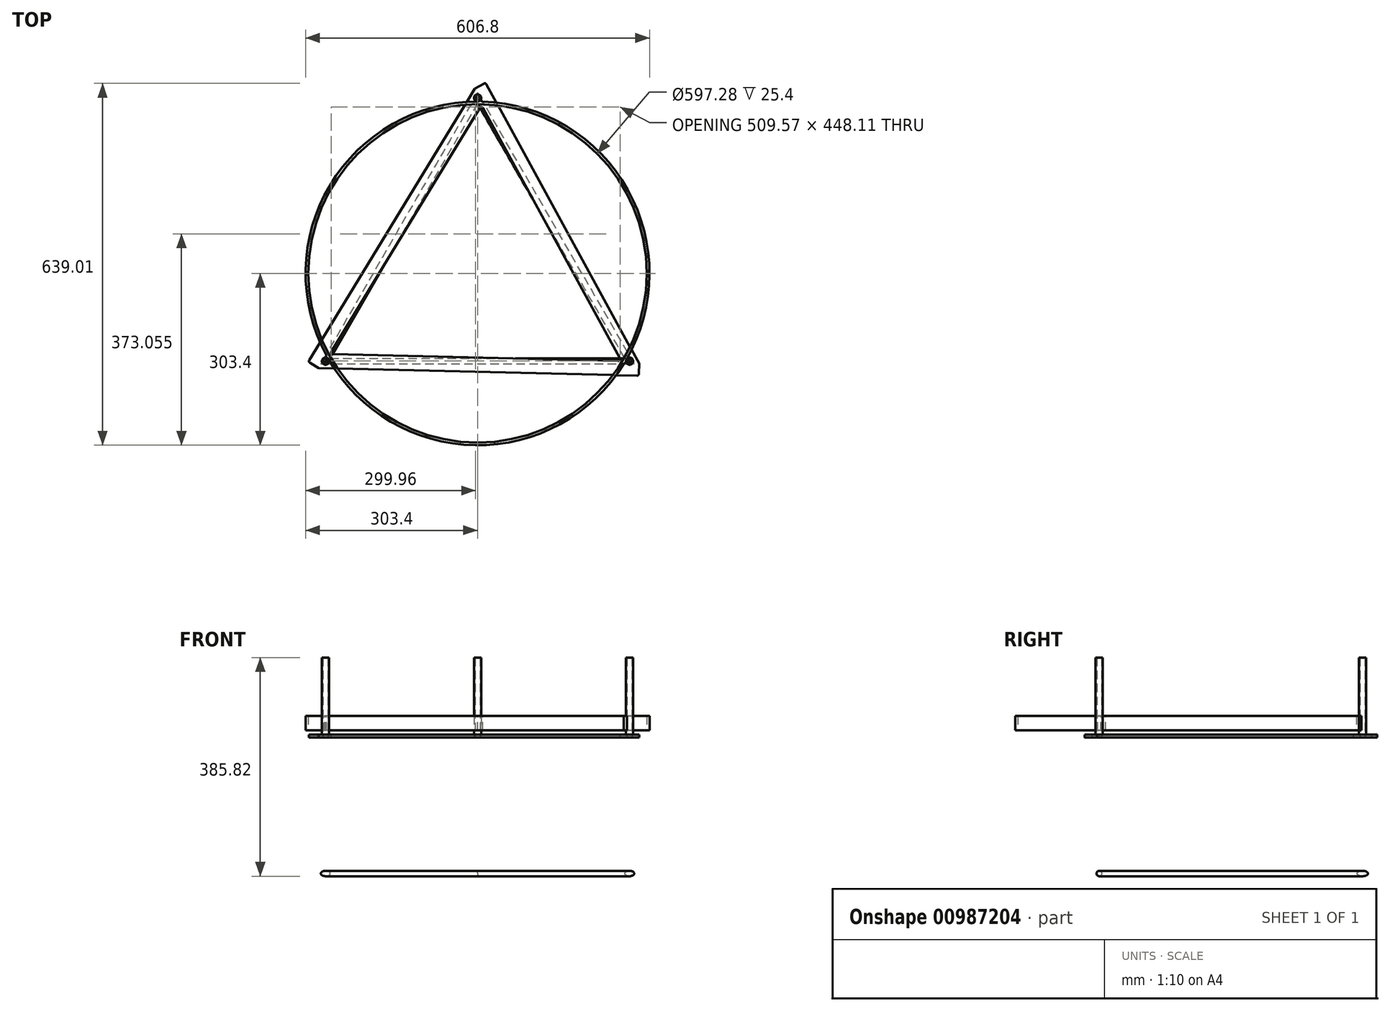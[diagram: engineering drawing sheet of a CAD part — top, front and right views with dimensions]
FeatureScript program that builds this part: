
annotation { "Feature Type Name" : "Feature", "Feature Type Description" : "" }
export const myFeature = defineFeature(function(context is Context, id is Id, definition is map)
    precondition{}
    {
        {
            var Q0;
            Q0=qCreatedBy(makeId("Top.planeOp"),FACE);
            var sketch = newSketch(context, id + "F0", { "sketchPlane" : qUnion([Q0])});
            skCircle(sketch, "E0", {"center": v(0, 0) * mm, "radius": 303.4 * mm});
            skCircle(sketch, "E1.0", {"center": v(0, 0) * mm, "radius": 298.64 * mm});
            skSolve(sketch);
        }
        {
            var Q0;
            Q0=makeQuery(id+"F0.imprint","IMPRINT",FACE,{"disambiguationData":[TD([[makeQuery(id+"F0.imprint","IMPRINT",EDGE,{"derivedFrom":sQuery(id+"F0.wireOp",EDGE,"E0")}),1.0]])]});
            extrude(context, id + "F1", {"entities" : qUnion([Q0]), "depth" : 25.4 * mm, "offsetDistance" : 25.4 * mm});
        }
        {
            var Q0;
            Q0=makeQuery(id+"F1.opExtrude","CAP_FACE",FACE,{"disambiguationData":[OSD([sQuery(id+"F0.wireOp",EDGE,"E0"),sQuery(id+"F0.wireOp",EDGE,"E1.0")])],"isStart":false});
            var sketch = newSketch(context, id + "F2", { "sketchPlane" : qUnion([Q0])});
            skLineSegment(sketch, "E2", {"start": v(0, 0) * mm, "end": v(0, 365.8) * mm});
            skLineSegment(sketch, "E3.1.0", {"start": v(0, 0) * mm, "end": v(-316.8, -182.9) * mm});
            skLineSegment(sketch, "E3.2.0", {"start": v(0, 0) * mm, "end": v(316.8, -182.9) * mm});
            skPoint(sketch, "E3.center", {"position": v(0, 0) * mm});
            skCircle(sketch, "E4", {"center": v(0, 309.75) * mm, "radius": 6.35 * mm});
            skCircle(sketch, "E5.1.0", {"center": v(-268.25, -154.88) * mm, "radius": 6.35 * mm});
            skCircle(sketch, "E5.2.0", {"center": v(268.25, -154.88) * mm, "radius": 6.35 * mm});
            skCircle(sketch, "E6.0", {"center": v(0, 309.75) * mm, "radius": 4.32 * mm});
            skCircle(sketch, "E7.1.0", {"center": v(-268.25, -154.88) * mm, "radius": 4.32 * mm});
            skCircle(sketch, "E7.2.0", {"center": v(268.25, -154.88) * mm, "radius": 4.32 * mm});
            skSolve(sketch);
        }
        {
            var Q0;
            {var subQ1=sQuery(id+"F2.wireOp",EDGE,"E2");var subQ3=sQuery(id+"F2.wireOp",EDGE,"E4");var subQ5=makeQuery(id+"F2.imprint","INTERSECT",VERTEX,{"derivedFrom":[subQ1,subQ3]});Q0=makeQuery(id+"F2.imprint","IMPRINT",FACE,{"disambiguationData":[TD([[makeQuery(id+"F2.imprint","IMPRINT",EDGE,{"disambiguationData":[TD([[subQ5,1.0]])],"derivedFrom":subQ1}),1.0]])]});}
            var Q1;
            {var subQ1=sQuery(id+"F2.wireOp",EDGE,"E2");var subQ3=sQuery(id+"F2.wireOp",EDGE,"E4");var subQ6=makeQuery(id+"F2.imprint","INTERSECT",VERTEX,{"derivedFrom":[subQ1,subQ3]});Q1=makeQuery(id+"F2.imprint","IMPRINT",FACE,{"disambiguationData":[TD([[makeQuery(id+"F2.imprint","IMPRINT",EDGE,{"disambiguationData":[TD([[subQ6,1.0]])],"derivedFrom":subQ1}),-1.0]])]});}
            var Q2;
            {var subQ1=sQuery(id+"F2.wireOp",EDGE,"E3.2.0");var subQ3=sQuery(id+"F2.wireOp",EDGE,"E5.2.0");var subQ5=makeQuery(id+"F2.imprint","INTERSECT",VERTEX,{"derivedFrom":[subQ1,subQ3]});Q2=makeQuery(id+"F2.imprint","IMPRINT",FACE,{"disambiguationData":[TD([[makeQuery(id+"F2.imprint","IMPRINT",EDGE,{"disambiguationData":[TD([[subQ5,1.0]])],"derivedFrom":subQ1}),-1.0]])]});}
            var Q3;
            {var subQ1=sQuery(id+"F2.wireOp",EDGE,"E3.2.0");var subQ3=sQuery(id+"F2.wireOp",EDGE,"E5.2.0");var subQ5=makeQuery(id+"F2.imprint","INTERSECT",VERTEX,{"derivedFrom":[subQ1,subQ3]});Q3=makeQuery(id+"F2.imprint","IMPRINT",FACE,{"disambiguationData":[TD([[makeQuery(id+"F2.imprint","IMPRINT",EDGE,{"disambiguationData":[TD([[subQ5,1.0]])],"derivedFrom":subQ1}),1.0]])]});}
            var Q4;
            {var subQ1=sQuery(id+"F2.wireOp",EDGE,"E3.1.0");var subQ3=sQuery(id+"F2.wireOp",EDGE,"E5.1.0");var subQ5=makeQuery(id+"F2.imprint","INTERSECT",VERTEX,{"derivedFrom":[subQ1,subQ3]});Q4=makeQuery(id+"F2.imprint","IMPRINT",FACE,{"disambiguationData":[TD([[makeQuery(id+"F2.imprint","IMPRINT",EDGE,{"disambiguationData":[TD([[subQ5,1.0]])],"derivedFrom":subQ1}),-1.0]])]});}
            var Q5;
            {var subQ1=sQuery(id+"F2.wireOp",EDGE,"E3.1.0");var subQ3=sQuery(id+"F2.wireOp",EDGE,"E5.1.0");var subQ5=makeQuery(id+"F2.imprint","INTERSECT",VERTEX,{"derivedFrom":[subQ1,subQ3]});Q5=makeQuery(id+"F2.imprint","IMPRINT",FACE,{"disambiguationData":[TD([[makeQuery(id+"F2.imprint","IMPRINT",EDGE,{"disambiguationData":[TD([[subQ5,1.0]])],"derivedFrom":subQ1}),1.0]])]});}
            extrude(context, id + "F3", {"entities" : qUnion([Q0, Q1, Q2, Q3, Q4, Q5]), "depth" : 103.12 * mm, "offsetDistance" : 25.4 * mm, "hasSecondDirection" : true, "secondDirectionOppositeDirection" : true, "secondDirectionDepth" : (33.13 - (3 / 16)) * mm});
        }
        {
            var Q0;
            Q0=makeQuery(id+"F1.opExtrude","CAP_FACE",FACE,{"disambiguationData":[OSD([sQuery(id+"F0.wireOp",EDGE,"E0"),sQuery(id+"F0.wireOp",EDGE,"E1.0")])],"isStart":false});
            var sketch = newSketch(context, id + "F4", { "sketchPlane" : qUnion([Q0])});
            skArc(sketch, "E8.0", {"start": v(-267.31, -143.52) * mm, "mid": v(-265.06, -147.63) * mm, "end": v(-262.75, -151.7) * mm});
            skCircle(sketch, "E9.0", {"center": v(-268.25, -154.88) * mm, "radius": 6.35 * mm});
            skLineSegment(sketch, "E10", {"start": v(-268.25, -154.88) * mm, "end": v(0, 0) * mm});
            skArc(sketch, "E11", {"start": v(-269.4, -148.63) * mm, "mid": v(-267.08, -146.6) * mm, "end": v(-267.3, -143.52) * mm});
            skLineSegment(sketch, "E12", {"start": v(-267.3, -143.52) * mm, "end": v(-267.31, -143.52) * mm});
            skLineSegment(sketch, "E13", {"start": v(-267.31, -143.52) * mm, "end": v(-267.3, -143.52) * mm});
            skLineSegment(sketch, "E14.MirrorCS", {"start": v(-257.95, -159.74) * mm, "end": v(-257.95, -159.74) * mm});
            skArc(sketch, "E15.MirrorCS", {"start": v(-263.42, -159) * mm, "mid": v(-260.5, -158) * mm, "end": v(-257.95, -159.74) * mm});
            skArc(sketch, "E16.MirrorCS", {"start": v(-257.95, -159.74) * mm, "mid": v(-260.38, -155.74) * mm, "end": v(-262.75, -151.7) * mm});
            skSolve(sketch);
        }
        {
            var Q0;
            {var subQ0=sQuery(id+"F4.wireOp",EDGE,"E9.0");var subQ1=sQuery(id+"F4.wireOp",EDGE,"E11");var subQ2=makeQuery(id+"F4.imprint","INTERSECT",VERTEX,{"derivedFrom":[subQ1,subQ0]});Q0=makeQuery(id+"F4.imprint","IMPRINT",FACE,{"disambiguationData":[TD([[makeQuery(id+"F4.imprint","IMPRINT",EDGE,{"disambiguationData":[TD([[subQ2,-1.0]])],"derivedFrom":subQ1}),-1.0]])]});}
            var Q1;
            {var subQ0=sQuery(id+"F4.wireOp",EDGE,"E9.0");var subQ1=sQuery(id+"F4.wireOp",EDGE,"E15.MirrorCS");var subQ2=makeQuery(id+"F4.imprint","INTERSECT",VERTEX,{"derivedFrom":[subQ1,subQ0]});Q1=makeQuery(id+"F4.imprint","IMPRINT",FACE,{"disambiguationData":[TD([[makeQuery(id+"F4.imprint","IMPRINT",EDGE,{"disambiguationData":[TD([[subQ2,-1.0]])],"derivedFrom":subQ1}),1.0]])]});}
            var Q2;
            Q2=makeQuery(id+"F1.opExtrude","CAP_FACE",FACE,{"disambiguationData":[OSD([sQuery(id+"F0.wireOp",EDGE,"E0"),sQuery(id+"F0.wireOp",EDGE,"E1.0")])],"isStart":true});
            extrude(context, id + "F5", {"entities" : qUnion([Q0, Q1]), "endBound" : BoundingType.UP_TO_SURFACE, "oppositeDirection" : true, "depth" : 25.4 * mm, "endBoundEntityFace" : qUnion([Q2]), "offsetDistance" : 25.4 * mm});
        }
        {
            var Q0;
            Q0=qCreatedBy(makeId("Right.planeOp"),FACE);
            var sketch = newSketch(context, id + "F6", { "sketchPlane" : qUnion([Q0])});
            skLineSegment(sketch, "E17", {"start": v(0, 0) * mm, "end": v(0, 80.11) * mm});
            skSolve(sketch);
        }
        {
            var Q0;
            Q0=makeQuery(id+"F5.opExtrude","SWEPT_BODY",BODY,{"disambiguationData":[OSD([sQuery(id+"F4.wireOp",EDGE,"E15.MirrorCS"),sQuery(id+"F4.wireOp",EDGE,"E16.MirrorCS"),sQuery(id+"F4.wireOp",EDGE,"E9.0")])]});
            var Q1;
            Q1=makeQuery(id+"F5.opExtrude","SWEPT_BODY",BODY,{"disambiguationData":[OSD([sQuery(id+"F4.wireOp",EDGE,"E11"),sQuery(id+"F4.wireOp",EDGE,"E8.0"),sQuery(id+"F4.wireOp",EDGE,"E9.0")])]});
            var Q2;
            Q2=sQuery(id+"F6.wireOp",EDGE,"E17");
            circularPattern(context, id + "F7", {"operationType" : NewBodyOperationType.ADD, "entities" : qUnion([Q0, Q1]), "axis" : qUnion([Q2]), "angle" : 360 * degree, "instanceCount" : 3, "equalSpace" : true});
        }
        {
            var Q0;
            Q0=makeQuery(id+"F3.opExtrude","CAP_FACE",FACE,{"disambiguationData":[OSD([sQuery(id+"F2.wireOp",EDGE,"E5.2.0"),sQuery(id+"F2.wireOp",EDGE,"E7.2.0")])],"isStart":true});
            var sketch = newSketch(context, id + "F8", { "sketchPlane" : qUnion([Q0])});
            skLineSegment(sketch, "E18.bottom", {"start": v(-280.31, 167.3) * mm, "end": v(281.35, 180.6) * mm});
            skLineSegment(sketch, "E18.top", {"start": v(-255.13, 142.48) * mm, "end": v(248.1, 154.4) * mm});
            skLineSegment(sketch, "E18.right", {"start": v(284.6, 177.5) * mm, "end": v(285.04, 159.11) * mm});
            skCircle(sketch, "E19.0", {"center": v(-268.25, 154.88) * mm, "radius": 4.32 * mm});
            skCircle(sketch, "E20.0", {"center": v(268.25, 154.88) * mm, "radius": 4.32 * mm});
            skPoint(sketch, "E21.center", {"position": v(3.6, 6.4) * mm});
            skLineSegment(sketch, "E22.1.0", {"start": v(4.17, -292.19) * mm, "end": v(-257.76, 137.66) * mm});
            skLineSegment(sketch, "E22.1.1", {"start": v(-4.72, -326.4) * mm, "end": v(-297.08, 153.36) * mm});
            skCircle(sketch, "E22.1.3", {"center": v(0, -309.75) * mm, "radius": 4.32 * mm});
            skLineSegment(sketch, "E22.1.4", {"start": v(-296.02, 157.73) * mm, "end": v(-280.31, 167.3) * mm});
            skLineSegment(sketch, "E22.2.0", {"start": v(250.96, 149.7) * mm, "end": v(9.67, -292.06) * mm});
            skLineSegment(sketch, "E22.2.1", {"start": v(285.04, 159.11) * mm, "end": v(15.72, -333.96) * mm});
            skCircle(sketch, "E22.2.2", {"center": v(0, -309.75) * mm, "radius": 4.32 * mm});
            skLineSegment(sketch, "E22.2.4", {"start": v(11.41, -335.22) * mm, "end": v(-4.72, -326.4) * mm});
            skPoint(sketch, "E22.center", {"position": v(0, 0) * mm});
            skPoint(sketch, "E23.orphan", {"position": v(-285.29, 167.18) * mm});
            skPoint(sketch, "E24.orphan", {"position": v(-277.04, 169.3) * mm});
            skLineSegment(sketch, "E25.trimOffspring", {"start": v(-268.25, 154.88) * mm, "end": v(-270.5, 158.56) * mm});
            skPoint(sketch, "E26.orphan", {"position": v(265.13, 175.65) * mm});
            skPoint(sketch, "E27.orphan", {"position": v(287.42, 163.48) * mm});
            skPoint(sketch, "E28.orphan", {"position": v(285.13, 155.28) * mm});
            skLineSegment(sketch, "E29.trimOffspring", {"start": v(268.25, 154.88) * mm, "end": v(272.57, 154.98) * mm});
            skPoint(sketch, "E30.orphan", {"position": v(19.56, -317.44) * mm});
            skLineSegment(sketch, "E31.trimOffspring", {"start": v(2.07, -305.96) * mm, "end": v(0, -309.75) * mm});
            skPoint(sketch, "E32.visualSharp", {"position": v(-260.62, 142.35) * mm});
            skArc(sketch, "E32.filletArc", {"start": v(-255.13, 142.48) * mm, "mid": v(-257.84, 140.83) * mm, "end": v(-257.76, 137.66) * mm});
            skPoint(sketch, "E33.visualSharp", {"position": v(-298.73, 156.07) * mm});
            skArc(sketch, "E33.filletArc", {"start": v(-296.02, 157.73) * mm, "mid": v(-297.45, 155.76) * mm, "end": v(-297.08, 153.36) * mm});
            skPoint(sketch, "E34.visualSharp", {"position": v(284.53, 180.67) * mm});
            skArc(sketch, "E34.filletArc", {"start": v(284.6, 177.5) * mm, "mid": v(283.62, 179.72) * mm, "end": v(281.35, 180.6) * mm});
            skPoint(sketch, "E35.visualSharp", {"position": v(253.6, 154.53) * mm});
            skArc(sketch, "E35.filletArc", {"start": v(250.96, 149.7) * mm, "mid": v(250.88, 152.88) * mm, "end": v(248.1, 154.4) * mm});
            skPoint(sketch, "E36.visualSharp", {"position": v(14.2, -336.74) * mm});
            skArc(sketch, "E36.filletArc", {"start": v(11.41, -335.22) * mm, "mid": v(13.83, -335.48) * mm, "end": v(15.72, -333.96) * mm});
            skPoint(sketch, "E37.visualSharp", {"position": v(7.03, -296.88) * mm});
            skArc(sketch, "E37.filletArc", {"start": v(4.17, -292.19) * mm, "mid": v(6.95, -293.7) * mm, "end": v(9.67, -292.06) * mm});
            skSolve(sketch);
        }
        {
            var Q0;
            Q0 = qSketchRegion(id + "F8", true);
            extrude(context, id + "F9", {"entities" : qUnion([Q0]), "operationType" : NewBodyOperationType.ADD, "depth" : 4.83 * mm, "offsetDistance" : 25.4 * mm});
        }
        {
            var Q0;
            Q0=makeQuery(id+"F9.opExtrude","CAP_FACE",FACE,{"disambiguationData":[OSD([sQuery(id+"F8.wireOp",EDGE,"E18.bottom"),sQuery(id+"F8.wireOp",EDGE,"E18.top"),sQuery(id+"F8.wireOp",EDGE,"E18.right"),sQuery(id+"F8.wireOp",EDGE,"E22.1.0"),sQuery(id+"F8.wireOp",EDGE,"E22.1.1"),sQuery(id+"F8.wireOp",EDGE,"E19.0"),sQuery(id+"F8.wireOp",EDGE,"E22.1.4"),sQuery(id+"F8.wireOp",EDGE,"E22.2.0"),sQuery(id+"F8.wireOp",EDGE,"E22.2.1"),sQuery(id+"F8.wireOp",EDGE,"E22.2.2"),sQuery(id+"F8.wireOp",EDGE,"E20.0"),sQuery(id+"F8.wireOp",EDGE,"E22.2.4"),sQuery(id+"F8.wireOp",EDGE,"E32.filletArc"),sQuery(id+"F8.wireOp",EDGE,"E33.filletArc"),sQuery(id+"F8.wireOp",EDGE,"E34.filletArc"),sQuery(id+"F8.wireOp",EDGE,"E35.filletArc"),sQuery(id+"F8.wireOp",EDGE,"E36.filletArc"),sQuery(id+"F8.wireOp",EDGE,"E37.filletArc")])],"isStart":false});
            cPlane(context, id + "F10", {"entities" : qUnion([Q0]), "cplaneType" : CPlaneType.OFFSET, "offset" : 563.63 * mm, "oppositeDirection" : true, "width" : 152.4 * mm, "height" : 152.4 * mm});
        }
        {
            var Q0;
            Q0=qCreatedBy(id+"F10.planeOp",FACE);
            var sketch = newSketch(context, id + "F11", { "sketchPlane" : qUnion([Q0])});
            skCircle(sketch, "E38.0", {"center": v(0, -309.75) * mm, "radius": 4.32 * mm});
            skCircle(sketch, "E39.0", {"center": v(-268.25, 154.88) * mm, "radius": 4.32 * mm});
            skCircle(sketch, "E40.0", {"center": v(268.25, 154.88) * mm, "radius": 4.32 * mm});
            skLineSegment(sketch, "E41", {"start": v(0, -309.75) * mm, "end": v(-268.25, 154.88) * mm});
            skLineSegment(sketch, "E42", {"start": v(268.25, 154.88) * mm, "end": v(-268.25, 154.88) * mm});
            skLineSegment(sketch, "E43", {"start": v(268.25, 154.88) * mm, "end": v(0, -309.75) * mm});
            skSolve(sketch);
        }
        {
            var Q0;
            Q0=qCreatedBy(makeId("Right.planeOp"),FACE);
            cPlane(context, id + "F12", {"entities" : qUnion([Q0]), "cplaneType" : CPlaneType.OFFSET, "offset" : 268.25 * mm, "width" : 152.4 * mm, "height" : 152.4 * mm});
        }
        {
            var Q0;
            Q0=qCreatedBy(id+"F12.planeOp",FACE);
            var sketch = newSketch(context, id + "F13", { "sketchPlane" : qUnion([Q0])});
            skPoint(sketch, "E44.0", {"position": v(-154.88, -252.54) * mm});
            skCircle(sketch, "E45", {"center": v(-154.88, -252.54) * mm, "radius": 4.76 * mm});
            skSolve(sketch);
        }
        {
            var Q0;
            Q0 = qSketchRegion(id + "F13", true);
            var Q1;
            Q1=sQuery(id+"F11.wireOp",EDGE,"E42");
            var Q2;
            Q2=sQuery(id+"F11.wireOp",EDGE,"E41");
            var Q3;
            Q3=sQuery(id+"F11.wireOp",EDGE,"E43");
            sweep(context, id + "F14", {"operationType" : NewBodyOperationType.ADD, "profiles" : qUnion([Q0]), "path" : qUnion([Q1, Q2, Q3])});
        }
    });
